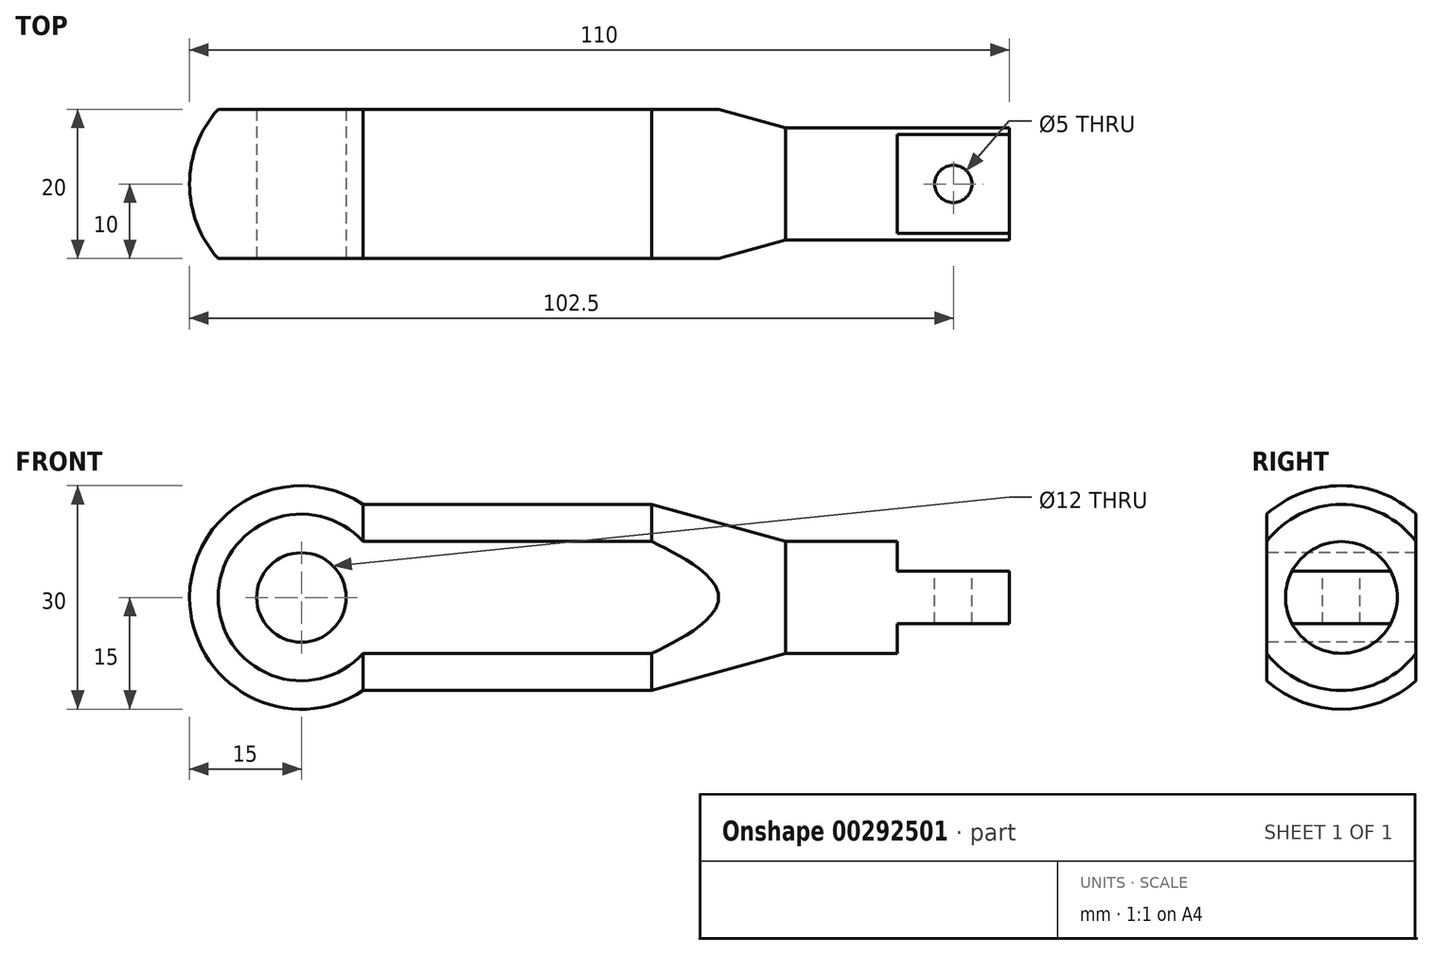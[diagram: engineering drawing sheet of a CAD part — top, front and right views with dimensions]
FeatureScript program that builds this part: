
annotation { "Feature Type Name" : "Feature", "Feature Type Description" : "" }
export const myFeature = defineFeature(function(context is Context, id is Id, definition is map)
    precondition{}
    {
        {
            var Q0;
            Q0=qCreatedBy(makeId("Front.planeOp"),FACE);
            var sketch = newSketch(context, id + "F0", { "sketchPlane" : qUnion([Q0])});
            skLineSegment(sketch, "E0", {"start": v(0, 0) * mm, "end": v(95.02, 0) * mm, "construction": true});
            skArc(sketch, "E1", {"start": v(-15, 0) * mm, "mid": v(-7.1, 13.22) * mm, "end": v(8.3, 12.5) * mm});
            skLineSegment(sketch, "E2", {"start": v(8.3, 12.5) * mm, "end": v(47, 12.5) * mm});
            skLineSegment(sketch, "E3", {"start": v(47, 12.5) * mm, "end": v(65, 7.5) * mm});
            skLineSegment(sketch, "E4", {"start": v(65, 7.5) * mm, "end": v(95, 7.5) * mm});
            skLineSegment(sketch, "E5", {"start": v(95, 7.5) * mm, "end": v(95, 0) * mm});
            skLineSegment(sketch, "E6", {"start": v(95, 0) * mm, "end": v(-15, 0) * mm});
            skSolve(sketch);
        }
        {
            var Q0;
            Q0 = qSketchRegion(id + "F0", true);
            var Q1;
            Q1=sQuery(id+"F0.wireOp",EDGE,"E6");
            revolve(context, id + "F1", {"entities" : qUnion([Q0]), "axis" : qUnion([Q1]), "revolveType" : RevolveType.FULL});
        }
        {
            var Q0;
            Q0=qCreatedBy(makeId("Front.planeOp"),FACE);
            var sketch = newSketch(context, id + "F2", { "sketchPlane" : qUnion([Q0])});
            skLineSegment(sketch, "E7", {"start": v(95, -7.5) * mm, "end": v(65, -7.5) * mm});
            skLineSegment(sketch, "E8", {"start": v(65, 7.5) * mm, "end": v(95, 7.5) * mm});
            skLineSegment(sketch, "E9.bottom", {"start": v(95, 7.5) * mm, "end": v(80, 7.5) * mm});
            skLineSegment(sketch, "E9.top", {"start": v(95, 3.5) * mm, "end": v(80, 3.5) * mm});
            skLineSegment(sketch, "E9.left", {"start": v(95, 7.5) * mm, "end": v(95, 3.5) * mm});
            skLineSegment(sketch, "E9.right", {"start": v(80, 7.5) * mm, "end": v(80, 3.5) * mm});
            skLineSegment(sketch, "E10", {"start": v(72.86, 0) * mm, "end": v(99.4, 0) * mm, "construction": true});
            skLineSegment(sketch, "E11.MirrorCS", {"start": v(80, -7.5) * mm, "end": v(80, -3.5) * mm});
            skLineSegment(sketch, "E12.MirrorCS", {"start": v(95, -7.5) * mm, "end": v(95, -3.5) * mm});
            skLineSegment(sketch, "E13.MirrorCS", {"start": v(95, -7.5) * mm, "end": v(80, -7.5) * mm});
            skLineSegment(sketch, "E14.MirrorCS", {"start": v(95, -3.5) * mm, "end": v(80, -3.5) * mm});
            skSolve(sketch);
        }
        {
            var Q0;
            Q0 = qSketchRegion(id + "F2", true);
            extrude(context, id + "F3", {"entities" : qUnion([Q0]), "operationType" : NewBodyOperationType.REMOVE, "endBound" : BoundingType.THROUGH_ALL, "depth" : 25 * mm, "hasSecondDirection" : true, "secondDirectionBound" : SecondDirectionBoundingType.THROUGH_ALL, "secondDirectionOppositeDirection" : true, "secondDirectionDepth" : 25 * mm});
        }
        {
            var Q0;
            Q0=makeQuery(id+"F1.opRevolve","SWEPT_FACE",FACE,{"disambiguationData":[OSD([sQuery(id+"F0.wireOp",EDGE,"E5")])]});
            var sketch = newSketch(context, id + "F4", { "sketchPlane" : qUnion([Q0])});
            skCircle(sketch, "E15", {"center": v(0, 0) * mm, "radius": 15 * mm});
            skLineSegment(sketch, "E16", {"start": v(-10, 11.18) * mm, "end": v(-10, -11.18) * mm});
            skLineSegment(sketch, "E17", {"start": v(10, 11.18) * mm, "end": v(10, -11.18) * mm});
            skLineSegment(sketch, "E18", {"start": v(0, -0.33) * mm, "end": v(0, 15.67) * mm, "construction": true});
            skSolve(sketch);
        }
        {
            var Q0;
            {var subQ0=sQuery(id+"F4.wireOp",EDGE,"E16");Q0=makeQuery(id+"F4.imprint","IMPRINT",FACE,{"disambiguationData":[TD([[makeQuery(id+"F4.imprint","IMPRINT",EDGE,{"derivedFrom":subQ0}),-1.0]])]});}
            var Q1;
            {var subQ0=sQuery(id+"F4.wireOp",EDGE,"E17");Q1=makeQuery(id+"F4.imprint","IMPRINT",FACE,{"disambiguationData":[TD([[makeQuery(id+"F4.imprint","IMPRINT",EDGE,{"derivedFrom":subQ0}),1.0]])]});}
            extrude(context, id + "F5", {"entities" : qUnion([Q0, Q1]), "operationType" : NewBodyOperationType.REMOVE, "endBound" : BoundingType.THROUGH_ALL, "oppositeDirection" : true, "depth" : 25 * mm});
        }
        {
            var Q0;
            Q0=makeQuery(id+"F5.boolean.opBoolean","COPY",FACE,{"derivedFrom":makeQuery(id+"F5.opExtrude","SWEPT_FACE",FACE,{"disambiguationData":[OSD([sQuery(id+"F4.wireOp",EDGE,"E16")])]})});
            var sketch = newSketch(context, id + "F6", { "sketchPlane" : qUnion([Q0])});
            skCircle(sketch, "E19", {"center": v(0, 0) * mm, "radius": 6 * mm});
            skSolve(sketch);
        }
        {
            var Q0;
            Q0=makeQuery(id+"F6.imprint","IMPRINT",FACE,{"disambiguationData":[TD([[makeQuery(id+"F6.imprint","IMPRINT",EDGE,{"derivedFrom":sQuery(id+"F6.wireOp",EDGE,"E19")}),1.0]])]});
            extrude(context, id + "F7", {"entities" : qUnion([Q0]), "operationType" : NewBodyOperationType.REMOVE, "endBound" : BoundingType.THROUGH_ALL, "oppositeDirection" : true, "depth" : 25 * mm});
        }
        {
            var Q0;
            Q0=makeQuery(id+"F3.boolean.opBoolean","COPY",FACE,{"derivedFrom":makeQuery(id+"F3.opExtrude","SWEPT_FACE",FACE,{"disambiguationData":[OSD([sQuery(id+"F2.wireOp",EDGE,"E9.top")])]})});
            var sketch = newSketch(context, id + "F8", { "sketchPlane" : qUnion([Q0])});
            skCircle(sketch, "E20", {"center": v(87.5, 0) * mm, "radius": 2.5 * mm});
            skSolve(sketch);
        }
        {
            var Q0;
            Q0 = qSketchRegion(id + "F8", true);
            extrude(context, id + "F9", {"entities" : qUnion([Q0]), "operationType" : NewBodyOperationType.REMOVE, "endBound" : BoundingType.THROUGH_ALL, "oppositeDirection" : true, "depth" : 25 * mm});
        }
    });
